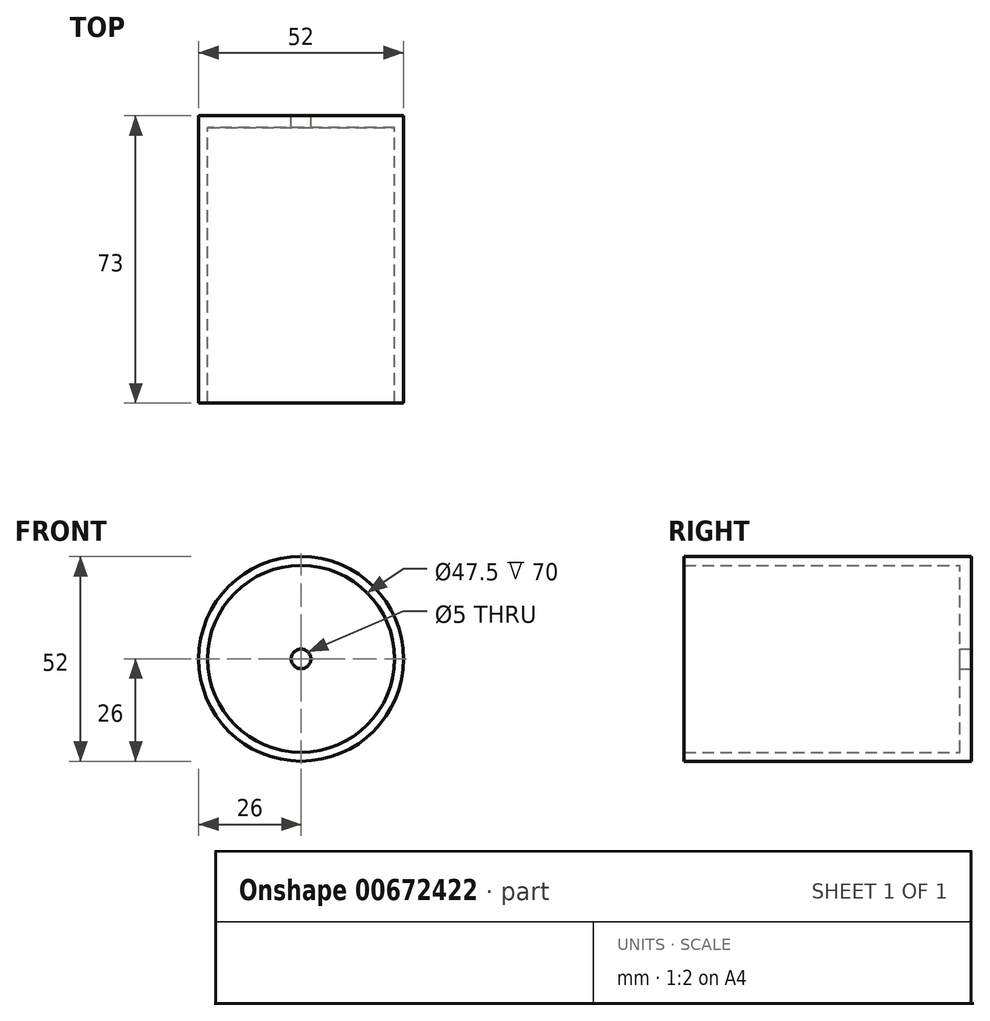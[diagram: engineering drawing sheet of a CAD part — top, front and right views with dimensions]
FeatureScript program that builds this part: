
annotation { "Feature Type Name" : "Feature", "Feature Type Description" : "" }
export const myFeature = defineFeature(function(context is Context, id is Id, definition is map)
    precondition{}
    {
        {
            var Q0;
            Q0=qCreatedBy(makeId("Front.planeOp"),FACE);
            var sketch = newSketch(context, id + "F0", { "sketchPlane" : qUnion([Q0])});
            skCircle(sketch, "E0", {"center": v(0, 0) * mm, "radius": 26 * mm});
            skSolve(sketch);
        }
        {
            var Q0;
            Q0=makeQuery(id+"F0.imprint","IMPRINT",FACE,{"disambiguationData":[TD([[makeQuery(id+"F0.imprint","IMPRINT",EDGE,{"derivedFrom":sQuery(id+"F0.wireOp",EDGE,"E0")}),1.0]])]});
            extrude(context, id + "F1", {"entities" : qUnion([Q0]), "depth" : 3 * mm, "offsetDistance" : 25 * mm});
        }
        {
            var Q0;
            Q0=makeQuery(id+"F1.opExtrude","CAP_FACE",FACE,{"disambiguationData":[OSD([sQuery(id+"F0.wireOp",EDGE,"E0")])],"isStart":false});
            var sketch = newSketch(context, id + "F2", { "sketchPlane" : qUnion([Q0])});
            skCircle(sketch, "E1", {"center": v(0, 0) * mm, "radius": 23.75 * mm});
            skSolve(sketch);
        }
        {
            var Q0;
            Q0=makeQuery(id+"F2.imprint","IMPRINT",FACE,{"disambiguationData":[TD([[makeQuery(id+"F2.imprint","IMPRINT",EDGE,{"derivedFrom":sQuery(id+"F2.wireOp",EDGE,"E1")}),-1.0]])]});
            extrude(context, id + "F3", {"entities" : qUnion([Q0]), "operationType" : NewBodyOperationType.ADD, "depth" : 70 * mm, "offsetDistance" : 25 * mm});
        }
        {
            var Q0;
            Q0=makeQuery(id+"F1.opExtrude","CAP_FACE",FACE,{"disambiguationData":[OSD([sQuery(id+"F0.wireOp",EDGE,"E0")])],"isStart":true});
            var sketch = newSketch(context, id + "F4", { "sketchPlane" : qUnion([Q0])});
            skPoint(sketch, "E2", {"position": v(0, 0) * mm});
            skSolve(sketch);
        }
        {
            var Q0;
            Q0=sQuery(id+"F4.wireOp",VERTEX,"E2");
            var Q1;
            Q1=makeQuery(id+"F1.opExtrude","SWEPT_BODY",BODY,{"disambiguationData":[OSD([sQuery(id+"F0.wireOp",EDGE,"E0")])]});
            hole(context, id + "F5", {"style" : HoleStyle.SIMPLE, "endStyle" : HoleEndStyle.THROUGH, "holeDiameter" : 5 * mm, "majorDiameter" : 5 * mm, "isTappedThrough" : true, "tappedDepth" : 12 * mm, "tapClearance" : 3, "startFromSketch" : true, "locations" : qUnion([Q0]), "scope" : qUnion([Q1])});
        }
    });
